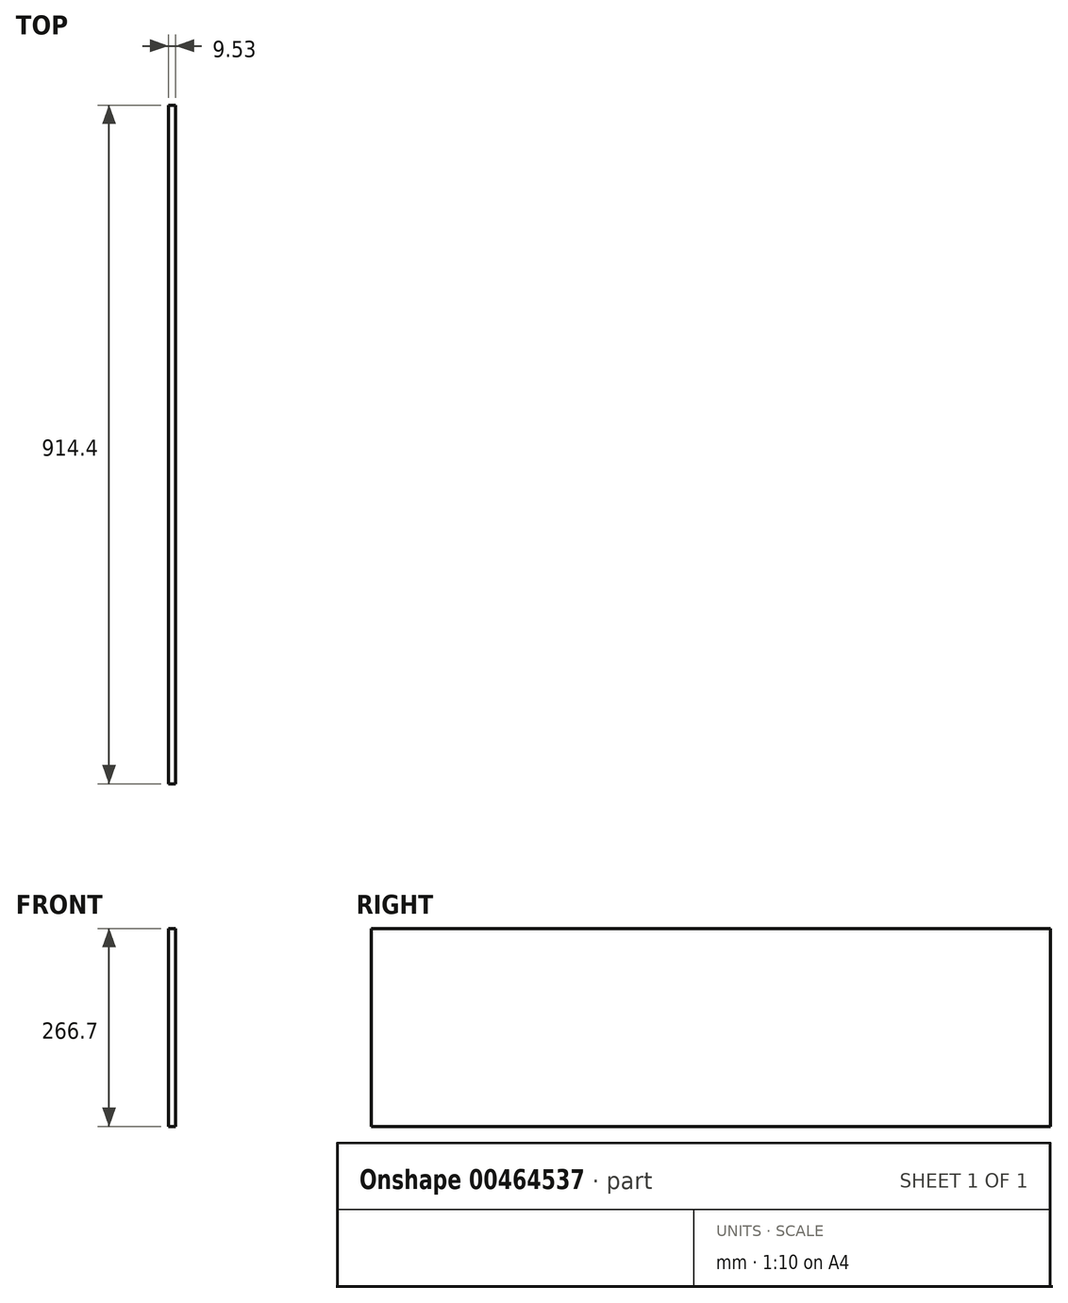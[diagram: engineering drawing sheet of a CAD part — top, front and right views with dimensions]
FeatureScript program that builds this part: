
annotation { "Feature Type Name" : "Feature", "Feature Type Description" : "" }
export const myFeature = defineFeature(function(context is Context, id is Id, definition is map)
    precondition{}
    {
        {
            var Q0;
            Q0=qCreatedBy(makeId("Right.planeOp"),FACE);
            var sketch = newSketch(context, id + "F0", { "sketchPlane" : qUnion([Q0])});
            skLineSegment(sketch, "E0.bottom", {"start": v(457.2, -133.35) * mm, "end": v(-457.2, -133.35) * mm});
            skLineSegment(sketch, "E0.top", {"start": v(457.2, 133.35) * mm, "end": v(-457.2, 133.35) * mm});
            skLineSegment(sketch, "E0.left", {"start": v(457.2, -133.35) * mm, "end": v(457.2, 133.35) * mm});
            skLineSegment(sketch, "E0.right", {"start": v(-457.2, -133.35) * mm, "end": v(-457.2, 133.35) * mm});
            skPoint(sketch, "E0.middle", {"position": v(0, 0) * mm});
            skSolve(sketch);
        }
        {
            var Q0;
            Q0 = qSketchRegion(id + "F0", true);
            extrude(context, id + "F1", {"entities" : qUnion([Q0]), "depth" : 9.52 * mm});
        }
    });
